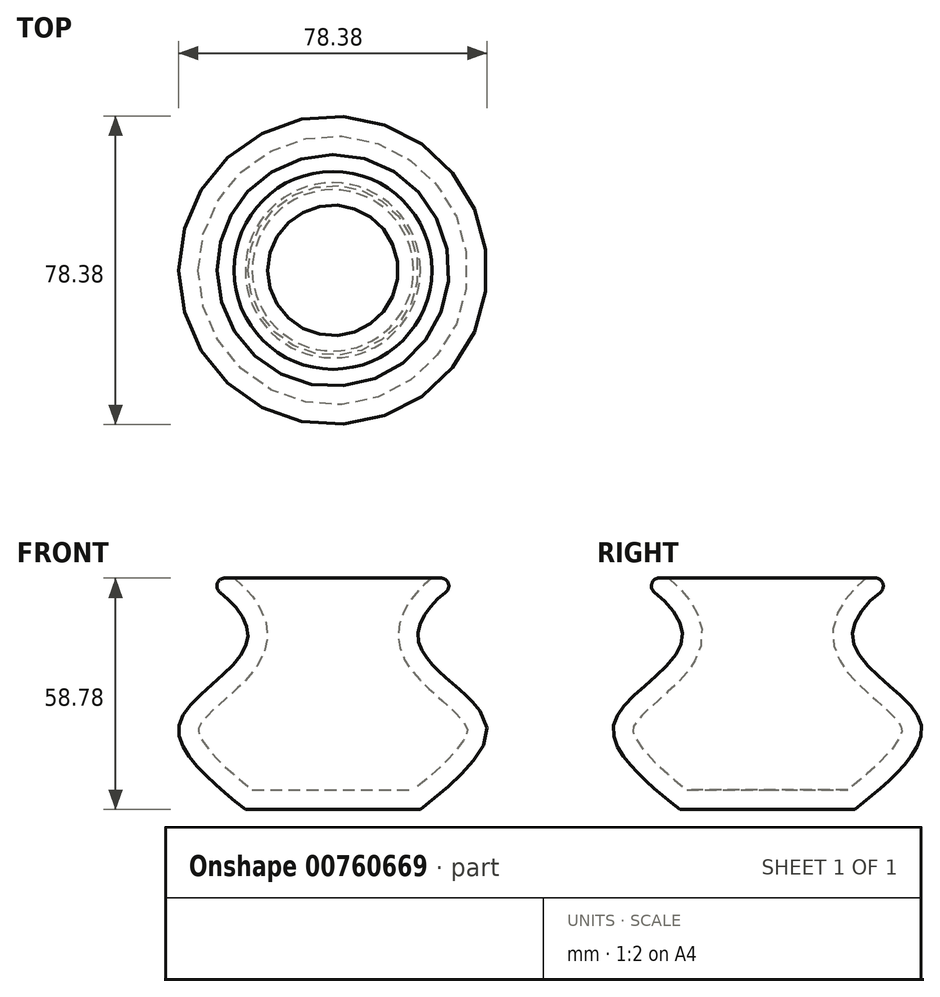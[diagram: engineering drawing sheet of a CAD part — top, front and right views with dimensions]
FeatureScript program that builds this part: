
annotation { "Feature Type Name" : "Feature", "Feature Type Description" : "" }
export const myFeature = defineFeature(function(context is Context, id is Id, definition is map)
    precondition{}
    {
        {
            var Q0;
            Q0=qCreatedBy(makeId("Front.planeOp"),FACE);
            var sketch = newSketch(context, id + "F0", { "sketchPlane" : qUnion([Q0])});
            skLineSegment(sketch, "E0", {"start": v(0, 0) * mm, "end": v(0, 61.61) * mm});
            skFitSpline(sketch, "E1", {"points": [v(34.98, 58.78) * mm, v(28.19, 54.81) * mm, v(21.67, 45.47) * mm, v(26.49, 35.55) * mm, v(38.95, 21.95) * mm, v(34.42, 10.9) * mm, v(22.24, 0) * mm], "startDerivative": vector(-50.3, -23.3) * mm, "endDerivative": vector(-68, -54.45) * mm});
            skFitSpline(sketch, "E2", {"points": [v(34.98, 58.78) * mm, v(0, 58.78) * mm], "startDerivative": vector(-34.98, 0) * mm, "endDerivative": vector(-34.98, 0) * mm});
            skLineSegment(sketch, "E3", {"start": v(22.24, 0) * mm, "end": v(0, 0) * mm});
            skSolve(sketch);
        }
        {
            var Q0;
            Q0=makeQuery(id+"F0.imprint","IMPRINT",FACE,{"disambiguationData":[TD([[makeQuery(id+"F0.imprint","IMPRINT",EDGE,{"derivedFrom":sQuery(id+"F0.wireOp",EDGE,"E1")}),-1.0]])]});
            var Q1;
            Q1=sQuery(id+"F0.wireOp",EDGE,"E0");
            revolve(context, id + "F1", {"surfaceOperationType" : NewSurfaceOperationType.NEW, "entities" : qUnion([Q0]), "axis" : qUnion([Q1]), "revolveType" : RevolveType.FULL});
        }
        {
            var Q0;
            Q0=makeQuery(id+"F1.opRevolve","SWEPT_EDGE",EDGE,{"disambiguationData":[OSD([sQuery(id+"F0.wireOp",EDGE,"E1"),sQuery(id+"F0.wireOp",EDGE,"E2")])]});
            fillet(context, id + "F2", {"entities" : qUnion([Q0]), "radius" : 2 * mm, "tangentPropagation" : true, "allowEdgeOverflow" : false});
        }
        {
            var Q0;
            Q0=makeQuery(id+"F1.opRevolve","SWEPT_FACE",FACE,{"disambiguationData":[OSD([sQuery(id+"F0.wireOp",EDGE,"E2")])]});
            shell(context, id + "F3", {"entities" : qUnion([Q0]), "thickness" : 5 * mm});
        }
    });
